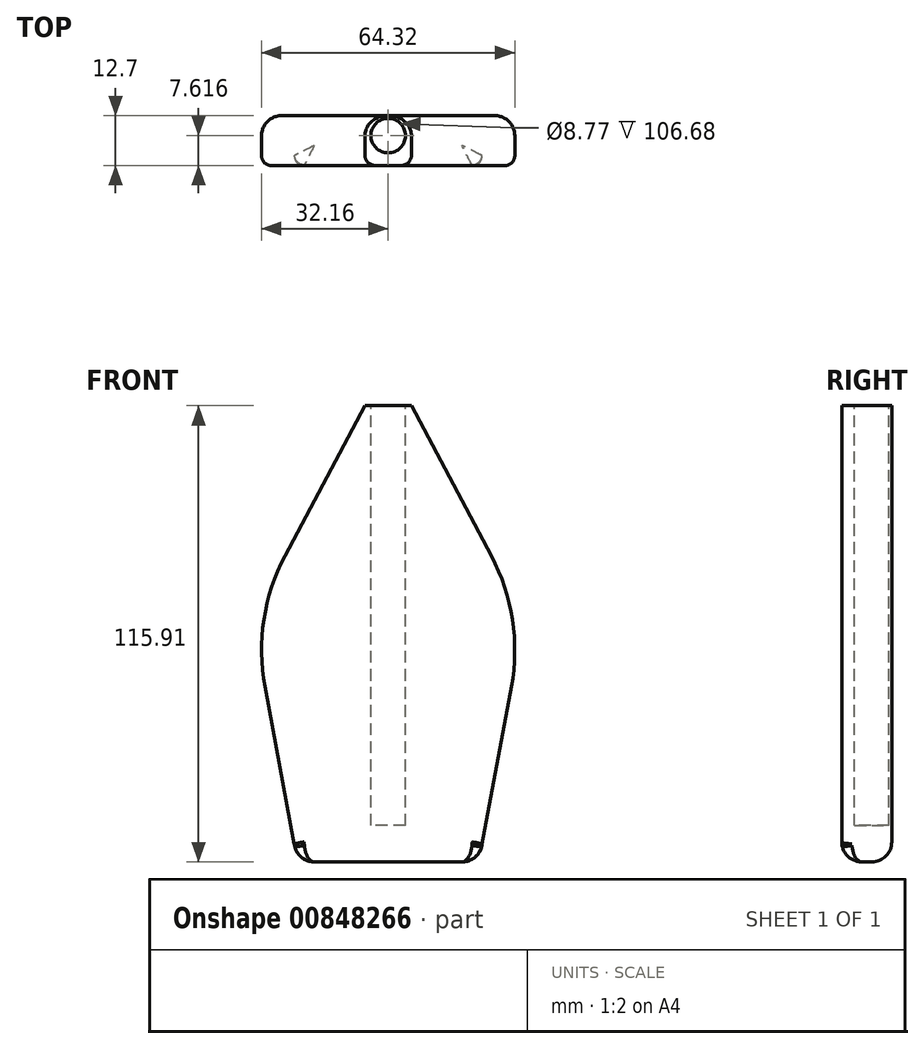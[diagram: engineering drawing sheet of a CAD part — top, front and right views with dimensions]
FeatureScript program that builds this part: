
annotation { "Feature Type Name" : "Feature", "Feature Type Description" : "" }
export const myFeature = defineFeature(function(context is Context, id is Id, definition is map)
    precondition{}
    {
        {
            var Q0;
            Q0=qCreatedBy(makeId("Front.planeOp"),FACE);
            var sketch = newSketch(context, id + "F0", { "sketchPlane" : qUnion([Q0])});
            skLineSegment(sketch, "E0", {"start": v(0, 0) * mm, "end": v(0, 127) * mm});
            skPoint(sketch, "E1.0.internal.orphan", {"position": v(17.13, 0) * mm});
            skLineSegment(sketch, "E2", {"start": v(0, 0) * mm, "end": v(23, 0) * mm});
            skLineSegment(sketch, "E3", {"start": v(23, 0) * mm, "end": v(31.3, 44.55) * mm});
            skLineSegment(sketch, "E4", {"start": v(26.21, 77.7) * mm, "end": v(0, 127) * mm});
            skPoint(sketch, "E5.visualSharp", {"position": v(34.56, 62.01) * mm});
            skArc(sketch, "E5.filletArc", {"start": v(31.3, 44.55) * mm, "mid": v(31.57, 61.55) * mm, "end": v(26.21, 77.7) * mm});
            skLineSegment(sketch, "E6.MirrorCS", {"start": v(-26.21, 77.7) * mm, "end": v(0, 127) * mm});
            skArc(sketch, "E7.MirrorCS", {"start": v(-31.3, 44.55) * mm, "mid": v(-31.57, 61.55) * mm, "end": v(-26.21, 77.7) * mm});
            skLineSegment(sketch, "E8.MirrorCS", {"start": v(-23, 0) * mm, "end": v(-31.3, 44.55) * mm});
            skLineSegment(sketch, "E9.MirrorCS", {"start": v(0, 0) * mm, "end": v(-23, 0) * mm});
            skSolve(sketch);
        }
        {
            var Q0;
            Q0 = qSketchRegion(id + "F0", true);
            extrude(context, id + "F1", {"entities" : qUnion([Q0]), "depth" : 12.7 * mm, "offsetDistance" : 25.4 * mm});
        }
        {
            var Q0;
            Q0=makeQuery(id+"F1.opExtrude","CAP_EDGE",EDGE,{"disambiguationData":[OSD([sQuery(id+"F0.wireOp",EDGE,"E4")])],"isStart":false});
            var Q1;
            Q1=makeQuery(id+"F1.opExtrude","CAP_EDGE",EDGE,{"disambiguationData":[OSD([sQuery(id+"F0.wireOp",EDGE,"E6.MirrorCS")])],"isStart":false});
            fillet(context, id + "F2", {"entities" : qUnion([Q0, Q1]), "radius" : 2.54 * mm, "tangentPropagation" : true, "allowEdgeOverflow" : false});
        }
        {
            var Q0;
            Q0=makeQuery(id+"F1.opExtrude","CAP_FACE",FACE,{"disambiguationData":[OSD([sQuery(id+"F0.wireOp",EDGE,"E2"),sQuery(id+"F0.wireOp",EDGE,"E3"),sQuery(id+"F0.wireOp",EDGE,"E4"),sQuery(id+"F0.wireOp",EDGE,"E5.filletArc"),sQuery(id+"F0.wireOp",EDGE,"E6.MirrorCS"),sQuery(id+"F0.wireOp",EDGE,"E7.MirrorCS"),sQuery(id+"F0.wireOp",EDGE,"E8.MirrorCS"),sQuery(id+"F0.wireOp",EDGE,"E9.MirrorCS")])],"isStart":true});
            fillet(context, id + "F3", {"entities" : qUnion([Q0]), "radius" : 5.08 * mm, "tangentPropagation" : true, "allowEdgeOverflow" : false});
        }
        {
            var Q0;
            Q0=makeQuery(id+"F1.opExtrude","CAP_EDGE",EDGE,{"disambiguationData":[OSD([sQuery(id+"F0.wireOp",EDGE,"E2"),sQuery(id+"F0.wireOp",EDGE,"E9.MirrorCS")])],"isStart":false});
            fillet(context, id + "F4", {"entities" : qUnion([Q0]), "radius" : 5.08 * mm, "tangentPropagation" : true, "allowEdgeOverflow" : false});
        }
        {
            var Q0;
            Q0=makeQuery(id+"F1.opExtrude","CAP_FACE",FACE,{"disambiguationData":[OSD([sQuery(id+"F0.wireOp",EDGE,"E2"),sQuery(id+"F0.wireOp",EDGE,"E3"),sQuery(id+"F0.wireOp",EDGE,"E4"),sQuery(id+"F0.wireOp",EDGE,"E5.filletArc"),sQuery(id+"F0.wireOp",EDGE,"E6.MirrorCS"),sQuery(id+"F0.wireOp",EDGE,"E7.MirrorCS"),sQuery(id+"F0.wireOp",EDGE,"E8.MirrorCS"),sQuery(id+"F0.wireOp",EDGE,"E9.MirrorCS")])],"isStart":false});
            var sketch = newSketch(context, id + "F5", { "sketchPlane" : qUnion([Q0])});
            skLineSegment(sketch, "E10", {"start": v(-3.02, 115.9) * mm, "end": v(3.02, 115.9) * mm});
            skLineSegment(sketch, "E11", {"start": v(3.02, 115.9) * mm, "end": v(0, 121.59) * mm});
            skLineSegment(sketch, "E12", {"start": v(0, 121.59) * mm, "end": v(-3.02, 115.9) * mm});
            skSolve(sketch);
        }
        {
            var Q0;
            Q0 = qSketchRegion(id + "F5", true);
            extrude(context, id + "F6", {"entities" : qUnion([Q0]), "operationType" : NewBodyOperationType.REMOVE, "oppositeDirection" : true, "depth" : 25.4 * mm, "offsetDistance" : 25.4 * mm});
        }
        {
            var Q0;
            Q0=makeQuery(id+"F1.opExtrude","CAP_FACE",FACE,{"disambiguationData":[OSD([sQuery(id+"F0.wireOp",EDGE,"E2"),sQuery(id+"F0.wireOp",EDGE,"E3"),sQuery(id+"F0.wireOp",EDGE,"E4"),sQuery(id+"F0.wireOp",EDGE,"E5.filletArc"),sQuery(id+"F0.wireOp",EDGE,"E6.MirrorCS"),sQuery(id+"F0.wireOp",EDGE,"E7.MirrorCS"),sQuery(id+"F0.wireOp",EDGE,"E8.MirrorCS"),sQuery(id+"F0.wireOp",EDGE,"E9.MirrorCS")])],"isStart":false});
            var sketch = newSketch(context, id + "F7", { "sketchPlane" : qUnion([Q0])});
            skLineSegment(sketch, "E13", {"start": v(5.9, 115.9) * mm, "end": v(-5.93, 115.9) * mm});
            skPoint(sketch, "E13.startSnap0", {"position": v(0, 115.9) * mm});
            skLineSegment(sketch, "E14", {"start": v(-5.93, 115.9) * mm, "end": v(0, 127.06) * mm});
            skLineSegment(sketch, "E15", {"start": v(0, 127.06) * mm, "end": v(5.9, 115.9) * mm});
            skSolve(sketch);
        }
        {
            var Q0;
            {var subQ0=sQuery(id+"F7.wireOp",EDGE,"E14");Q0=makeQuery(id+"F7.imprint","IMPRINT",FACE,{"disambiguationData":[TD([[makeQuery(id+"F7.imprint","IMPRINT",EDGE,{"derivedFrom":subQ0}),-1.0]])]});}
            extrude(context, id + "F8", {"entities" : qUnion([Q0]), "operationType" : NewBodyOperationType.REMOVE, "oppositeDirection" : true, "depth" : 25.4 * mm, "offsetDistance" : 25.4 * mm});
        }
        {
            var Q0;
            Q0=makeQuery(id+"F8.boolean.opBoolean","MERGE",FACE,{"derivedFrom":[makeQuery(id+"F6.boolean.opBoolean","COPY",FACE,{"derivedFrom":makeQuery(id+"F6.opExtrude","SWEPT_FACE",FACE,{"disambiguationData":[OSD([sQuery(id+"F5.wireOp",EDGE,"E10")])]})}),makeQuery(id+"F8.opExtrude","SWEPT_FACE",FACE,{"disambiguationData":[OSD([sQuery(id+"F7.wireOp",EDGE,"E13")])]})]});
            var sketch = newSketch(context, id + "F9", { "sketchPlane" : qUnion([Q0])});
            skCircle(sketch, "E16", {"center": v(0, -5.08) * mm, "radius": 4.39 * mm});
            skSolve(sketch);
        }
        {
            var Q0;
            Q0 = qSketchRegion(id + "F9", true);
            extrude(context, id + "F10", {"entities" : qUnion([Q0]), "operationType" : NewBodyOperationType.REMOVE, "oppositeDirection" : true, "depth" : 106.68 * mm, "offsetDistance" : 25.4 * mm});
        }
    });
